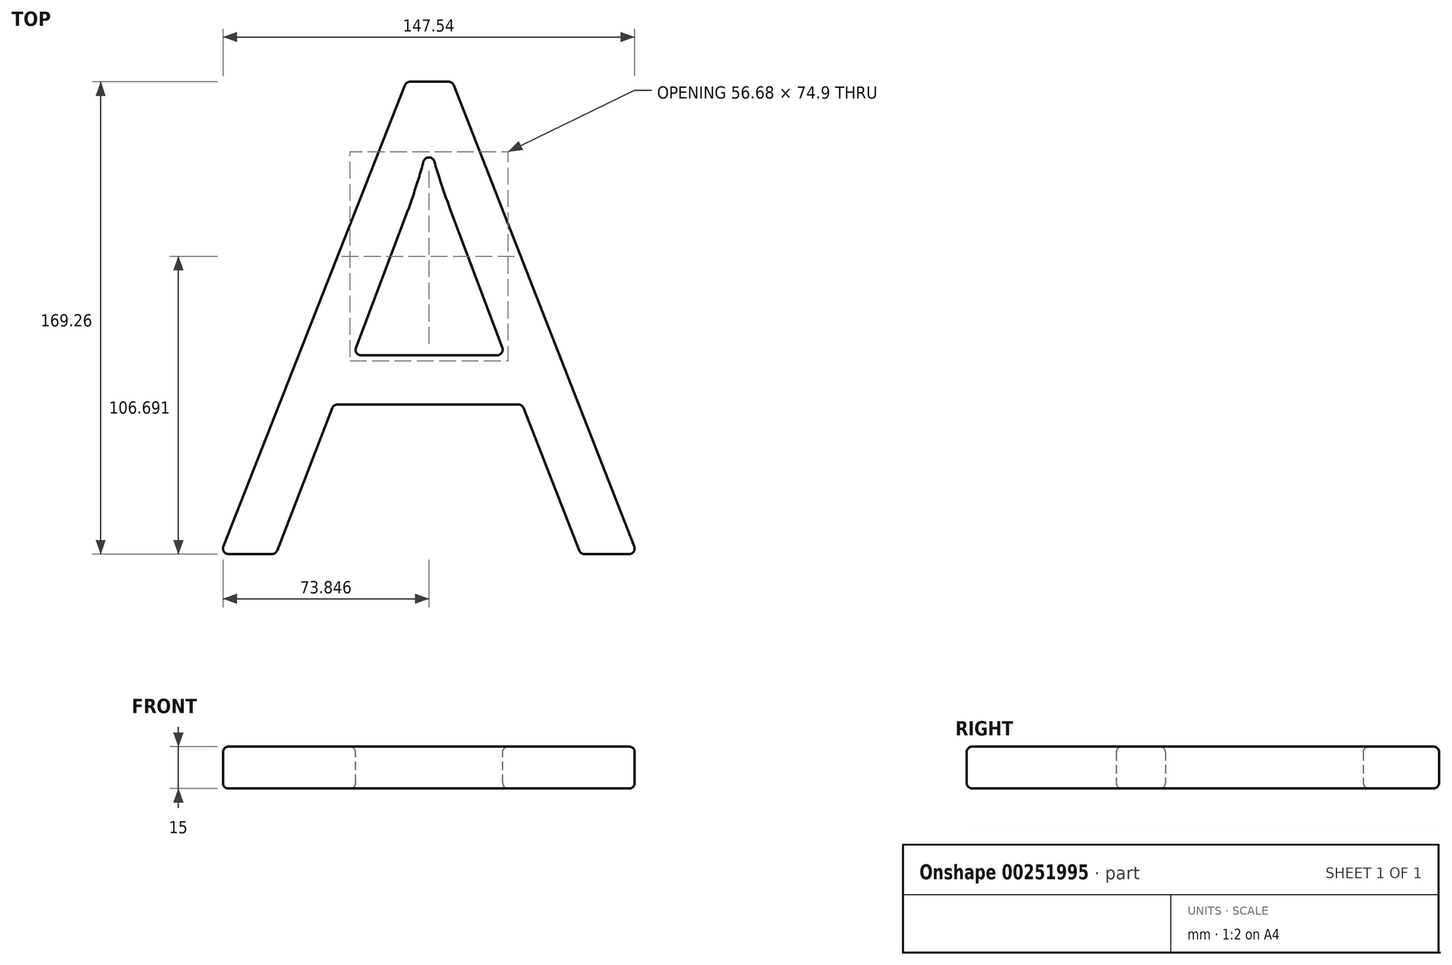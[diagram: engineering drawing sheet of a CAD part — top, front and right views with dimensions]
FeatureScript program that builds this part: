
annotation { "Feature Type Name" : "Feature", "Feature Type Description" : "" }
export const myFeature = defineFeature(function(context is Context, id is Id, definition is map)
    precondition{}
    {
        {
            var Q0;
            Q0=qCreatedBy(makeId("Top.planeOp"),FACE);
            var sketch = newSketch(context, id + "F0", { "sketchPlane" : qUnion([Q0])});
            skLineSegment(sketch, "E0", {"start": v(-70.15, 88.8) * mm, "end": v(95.11, 88.8) * mm, "construction": true});
            skLineSegment(sketch, "E1", {"start": v(-73.3, -81.2) * mm, "end": v(95.11, -81.2) * mm, "construction": true});
            skText(sketch, "E2", { "text": "A", "fontName": "OpenSans-Regular.ttf"});
            const initialGuessF0  = {"E2": [-0.04242, -0.0812, 1, 0, 0.17]};
            skSetInitialGuess(sketch, initialGuessF0);
            skSolve(sketch);
        }
        {
            var Q0;
            Q0 = qSketchRegion(id + "F0", true);
            extrude(context, id + "F1", {"entities" : qUnion([Q0]), "depth" : 15 * mm});
        }
        {
            var Q0;
            Q0=makeQuery(id+"F1.opExtrude","CAP_FACE",FACE,{"disambiguationData":[OSD([sQuery(id+"F0.wireOp",EDGE,"E2.sketch_text.stroke-0"),sQuery(id+"F0.wireOp",EDGE,"E2.sketch_text.stroke-1"),sQuery(id+"F0.wireOp",EDGE,"E2.sketch_text.stroke-2"),sQuery(id+"F0.wireOp",EDGE,"E2.sketch_text.stroke-3"),sQuery(id+"F0.wireOp",EDGE,"E2.sketch_text.stroke-4"),sQuery(id+"F0.wireOp",EDGE,"E2.sketch_text.stroke-5"),sQuery(id+"F0.wireOp",EDGE,"E2.sketch_text.stroke-6"),sQuery(id+"F0.wireOp",EDGE,"E2.sketch_text.stroke-7"),sQuery(id+"F0.wireOp",EDGE,"E2.sketch_text.stroke-8"),sQuery(id+"F0.wireOp",EDGE,"E2.sketch_text.stroke-9"),sQuery(id+"F0.wireOp",EDGE,"E2.sketch_text.stroke-10"),sQuery(id+"F0.wireOp",EDGE,"E2.sketch_text.stroke-11"),sQuery(id+"F0.wireOp",EDGE,"E2.sketch_text.stroke-12")])],"isStart":true});
            var Q1;
            Q1=makeQuery(id+"F1.opExtrude","CAP_FACE",FACE,{"disambiguationData":[OSD([sQuery(id+"F0.wireOp",EDGE,"E2.sketch_text.stroke-0"),sQuery(id+"F0.wireOp",EDGE,"E2.sketch_text.stroke-1"),sQuery(id+"F0.wireOp",EDGE,"E2.sketch_text.stroke-2"),sQuery(id+"F0.wireOp",EDGE,"E2.sketch_text.stroke-3"),sQuery(id+"F0.wireOp",EDGE,"E2.sketch_text.stroke-4"),sQuery(id+"F0.wireOp",EDGE,"E2.sketch_text.stroke-5"),sQuery(id+"F0.wireOp",EDGE,"E2.sketch_text.stroke-6"),sQuery(id+"F0.wireOp",EDGE,"E2.sketch_text.stroke-7"),sQuery(id+"F0.wireOp",EDGE,"E2.sketch_text.stroke-8"),sQuery(id+"F0.wireOp",EDGE,"E2.sketch_text.stroke-9"),sQuery(id+"F0.wireOp",EDGE,"E2.sketch_text.stroke-10"),sQuery(id+"F0.wireOp",EDGE,"E2.sketch_text.stroke-11"),sQuery(id+"F0.wireOp",EDGE,"E2.sketch_text.stroke-12")])],"isStart":false});
            var Q2;
            Q2=makeQuery(id+"F1.opExtrude","SWEPT_FACE",FACE,{"disambiguationData":[OSD([sQuery(id+"F0.wireOp",EDGE,"E2.sketch_text.stroke-1")])]});
            var Q3;
            Q3=makeQuery(id+"F1.opExtrude","SWEPT_EDGE",EDGE,{"disambiguationData":[OSD([sQuery(id+"F0.wireOp",EDGE,"E2.sketch_text.stroke-4"),sQuery(id+"F0.wireOp",EDGE,"E2.sketch_text.stroke-5")])]});
            var Q4;
            Q4=makeQuery(id+"F1.opExtrude","SWEPT_FACE",FACE,{"disambiguationData":[OSD([sQuery(id+"F0.wireOp",EDGE,"E2.sketch_text.stroke-5")])]});
            var Q5;
            Q5=makeQuery(id+"F1.opExtrude","SWEPT_FACE",FACE,{"disambiguationData":[OSD([sQuery(id+"F0.wireOp",EDGE,"E2.sketch_text.stroke-6")])]});
            var Q6;
            Q6=makeQuery(id+"F1.opExtrude","SWEPT_EDGE",EDGE,{"disambiguationData":[OSD([sQuery(id+"F0.wireOp",EDGE,"E2.sketch_text.stroke-5"),sQuery(id+"F0.wireOp",EDGE,"E2.sketch_text.stroke-6")])]});
            var Q7;
            Q7=makeQuery(id+"F1.opExtrude","SWEPT_FACE",FACE,{"disambiguationData":[OSD([sQuery(id+"F0.wireOp",EDGE,"E2.sketch_text.stroke-4")])]});
            var Q8;
            Q8=makeQuery(id+"F1.opExtrude","SWEPT_FACE",FACE,{"disambiguationData":[OSD([sQuery(id+"F0.wireOp",EDGE,"E2.sketch_text.stroke-8")])]});
            var Q9;
            Q9=makeQuery(id+"F1.opExtrude","SWEPT_FACE",FACE,{"disambiguationData":[OSD([sQuery(id+"F0.wireOp",EDGE,"E2.sketch_text.stroke-0")])]});
            var Q10;
            Q10=makeQuery(id+"F1.opExtrude","SWEPT_FACE",FACE,{"disambiguationData":[OSD([sQuery(id+"F0.wireOp",EDGE,"E2.sketch_text.stroke-12")])]});
            var Q11;
            Q11=makeQuery(id+"F1.opExtrude","SWEPT_FACE",FACE,{"disambiguationData":[OSD([sQuery(id+"F0.wireOp",EDGE,"E2.sketch_text.stroke-11")])]});
            var Q12;
            Q12=makeQuery(id+"F1.opExtrude","SWEPT_EDGE",EDGE,{"disambiguationData":[OSD([sQuery(id+"F0.wireOp",EDGE,"E2.sketch_text.stroke-6"),sQuery(id+"F0.wireOp",EDGE,"E2.sketch_text.stroke-7")])]});
            var Q13;
            Q13=makeQuery(id+"F1.opExtrude","SWEPT_EDGE",EDGE,{"disambiguationData":[OSD([sQuery(id+"F0.wireOp",EDGE,"E2.sketch_text.stroke-11"),sQuery(id+"F0.wireOp",EDGE,"E2.sketch_text.stroke-12")])]});
            var Q14;
            Q14=makeQuery(id+"F1.opExtrude","SWEPT_FACE",FACE,{"disambiguationData":[OSD([sQuery(id+"F0.wireOp",EDGE,"E2.sketch_text.stroke-10")])]});
            var Q15;
            Q15=makeQuery(id+"F1.opExtrude","CAP_EDGE",EDGE,{"disambiguationData":[OSD([sQuery(id+"F0.wireOp",EDGE,"E2.sketch_text.stroke-1")])],"isStart":false});
            var Q16;
            Q16=makeQuery(id+"F1.opExtrude","CAP_EDGE",EDGE,{"disambiguationData":[OSD([sQuery(id+"F0.wireOp",EDGE,"E2.sketch_text.stroke-9")])],"isStart":false});
            var Q17;
            Q17=makeQuery(id+"F1.opExtrude","CAP_EDGE",EDGE,{"disambiguationData":[OSD([sQuery(id+"F0.wireOp",EDGE,"E2.sketch_text.stroke-10")])],"isStart":false});
            var Q18;
            Q18=makeQuery(id+"F1.opExtrude","CAP_EDGE",EDGE,{"disambiguationData":[OSD([sQuery(id+"F0.wireOp",EDGE,"E2.sketch_text.stroke-11")])],"isStart":true});
            var Q19;
            Q19=makeQuery(id+"F1.opExtrude","CAP_EDGE",EDGE,{"disambiguationData":[OSD([sQuery(id+"F0.wireOp",EDGE,"E2.sketch_text.stroke-12")])],"isStart":true});
            var Q20;
            Q20=makeQuery(id+"F1.opExtrude","CAP_EDGE",EDGE,{"disambiguationData":[OSD([sQuery(id+"F0.wireOp",EDGE,"E2.sketch_text.stroke-4")])],"isStart":false});
            var Q21;
            Q21=makeQuery(id+"F1.opExtrude","CAP_EDGE",EDGE,{"disambiguationData":[OSD([sQuery(id+"F0.wireOp",EDGE,"E2.sketch_text.stroke-12")])],"isStart":false});
            var Q22;
            Q22=makeQuery(id+"F1.opExtrude","CAP_EDGE",EDGE,{"disambiguationData":[OSD([sQuery(id+"F0.wireOp",EDGE,"E2.sketch_text.stroke-5")])],"isStart":true});
            var Q23;
            Q23=makeQuery(id+"F1.opExtrude","CAP_EDGE",EDGE,{"disambiguationData":[OSD([sQuery(id+"F0.wireOp",EDGE,"E2.sketch_text.stroke-5")])],"isStart":false});
            var Q24;
            Q24=makeQuery(id+"F1.opExtrude","CAP_EDGE",EDGE,{"disambiguationData":[OSD([sQuery(id+"F0.wireOp",EDGE,"E2.sketch_text.stroke-7")])],"isStart":false});
            var Q25;
            Q25=makeQuery(id+"F1.opExtrude","SWEPT_EDGE",EDGE,{"disambiguationData":[OSD([sQuery(id+"F0.wireOp",EDGE,"E2.sketch_text.stroke-0"),sQuery(id+"F0.wireOp",EDGE,"E2.sketch_text.stroke-1")])]});
            var Q26;
            Q26=makeQuery(id+"F1.opExtrude","SWEPT_EDGE",EDGE,{"disambiguationData":[OSD([sQuery(id+"F0.wireOp",EDGE,"E2.sketch_text.stroke-1"),sQuery(id+"F0.wireOp",EDGE,"E2.sketch_text.stroke-2")])]});
            var Q27;
            Q27=makeQuery(id+"F1.opExtrude","SWEPT_EDGE",EDGE,{"disambiguationData":[OSD([sQuery(id+"F0.wireOp",EDGE,"E2.sketch_text.stroke-2"),sQuery(id+"F0.wireOp",EDGE,"E2.sketch_text.stroke-3")])]});
            var Q28;
            Q28=makeQuery(id+"F1.opExtrude","SWEPT_EDGE",EDGE,{"disambiguationData":[OSD([sQuery(id+"F0.wireOp",EDGE,"E2.sketch_text.stroke-3"),sQuery(id+"F0.wireOp",EDGE,"E2.sketch_text.stroke-4")])]});
            var Q29;
            Q29=makeQuery(id+"F1.opExtrude","SWEPT_FACE",FACE,{"disambiguationData":[OSD([sQuery(id+"F0.wireOp",EDGE,"E2.sketch_text.stroke-2")])]});
            var Q30;
            Q30=makeQuery(id+"F1.opExtrude","SWEPT_FACE",FACE,{"disambiguationData":[OSD([sQuery(id+"F0.wireOp",EDGE,"E2.sketch_text.stroke-3")])]});
            var Q31;
            Q31=makeQuery(id+"F1.opExtrude","SWEPT_EDGE",EDGE,{"disambiguationData":[OSD([sQuery(id+"F0.wireOp",EDGE,"E2.sketch_text.stroke-8"),sQuery(id+"F0.wireOp",EDGE,"E2.sketch_text.stroke-12")])]});
            var Q32;
            Q32=makeQuery(id+"F1.opExtrude","SWEPT_EDGE",EDGE,{"disambiguationData":[OSD([sQuery(id+"F0.wireOp",EDGE,"E2.sketch_text.stroke-0"),sQuery(id+"F0.wireOp",EDGE,"E2.sketch_text.stroke-7")])]});
            var Q33;
            Q33=makeQuery(id+"F1.opExtrude","CAP_EDGE",EDGE,{"disambiguationData":[OSD([sQuery(id+"F0.wireOp",EDGE,"E2.sketch_text.stroke-1")])],"isStart":true});
            var Q34;
            Q34=makeQuery(id+"F1.opExtrude","CAP_EDGE",EDGE,{"disambiguationData":[OSD([sQuery(id+"F0.wireOp",EDGE,"E2.sketch_text.stroke-0")])],"isStart":false});
            var Q35;
            Q35=makeQuery(id+"F1.opExtrude","CAP_EDGE",EDGE,{"disambiguationData":[OSD([sQuery(id+"F0.wireOp",EDGE,"E2.sketch_text.stroke-0")])],"isStart":true});
            var Q36;
            Q36=makeQuery(id+"F1.opExtrude","SWEPT_FACE",FACE,{"disambiguationData":[OSD([sQuery(id+"F0.wireOp",EDGE,"E2.sketch_text.stroke-7")])]});
            var Q37;
            Q37=makeQuery(id+"F1.opExtrude","SWEPT_EDGE",EDGE,{"disambiguationData":[OSD([sQuery(id+"F0.wireOp",EDGE,"E2.sketch_text.stroke-10"),sQuery(id+"F0.wireOp",EDGE,"E2.sketch_text.stroke-11")])]});
            var Q38;
            Q38=makeQuery(id+"F1.opExtrude","SWEPT_FACE",FACE,{"disambiguationData":[OSD([sQuery(id+"F0.wireOp",EDGE,"E2.sketch_text.stroke-9")])]});
            var Q39;
            Q39=makeQuery(id+"F1.opExtrude","CAP_EDGE",EDGE,{"disambiguationData":[OSD([sQuery(id+"F0.wireOp",EDGE,"E2.sketch_text.stroke-8")])],"isStart":true});
            var Q40;
            Q40=makeQuery(id+"F1.opExtrude","CAP_EDGE",EDGE,{"disambiguationData":[OSD([sQuery(id+"F0.wireOp",EDGE,"E2.sketch_text.stroke-8")])],"isStart":false});
            var Q41;
            Q41=makeQuery(id+"F1.opExtrude","CAP_EDGE",EDGE,{"disambiguationData":[OSD([sQuery(id+"F0.wireOp",EDGE,"E2.sketch_text.stroke-9")])],"isStart":true});
            var Q42;
            Q42=makeQuery(id+"F1.opExtrude","CAP_EDGE",EDGE,{"disambiguationData":[OSD([sQuery(id+"F0.wireOp",EDGE,"E2.sketch_text.stroke-2")])],"isStart":true});
            var Q43;
            Q43=makeQuery(id+"F1.opExtrude","CAP_EDGE",EDGE,{"disambiguationData":[OSD([sQuery(id+"F0.wireOp",EDGE,"E2.sketch_text.stroke-2")])],"isStart":false});
            var Q44;
            Q44=makeQuery(id+"F1.opExtrude","CAP_EDGE",EDGE,{"disambiguationData":[OSD([sQuery(id+"F0.wireOp",EDGE,"E2.sketch_text.stroke-3")])],"isStart":false});
            var Q45;
            Q45=makeQuery(id+"F1.opExtrude","CAP_EDGE",EDGE,{"disambiguationData":[OSD([sQuery(id+"F0.wireOp",EDGE,"E2.sketch_text.stroke-11")])],"isStart":false});
            var Q46;
            Q46=makeQuery(id+"F1.opExtrude","CAP_EDGE",EDGE,{"disambiguationData":[OSD([sQuery(id+"F0.wireOp",EDGE,"E2.sketch_text.stroke-4")])],"isStart":true});
            var Q47;
            Q47=makeQuery(id+"F1.opExtrude","CAP_EDGE",EDGE,{"disambiguationData":[OSD([sQuery(id+"F0.wireOp",EDGE,"E2.sketch_text.stroke-6")])],"isStart":true});
            var Q48;
            Q48=makeQuery(id+"F1.opExtrude","CAP_EDGE",EDGE,{"disambiguationData":[OSD([sQuery(id+"F0.wireOp",EDGE,"E2.sketch_text.stroke-6")])],"isStart":false});
            var Q49;
            Q49=makeQuery(id+"F1.opExtrude","CAP_EDGE",EDGE,{"disambiguationData":[OSD([sQuery(id+"F0.wireOp",EDGE,"E2.sketch_text.stroke-7")])],"isStart":true});
            var Q50;
            Q50=makeQuery(id+"F1.opExtrude","SWEPT_EDGE",EDGE,{"disambiguationData":[OSD([sQuery(id+"F0.wireOp",EDGE,"E2.sketch_text.stroke-8"),sQuery(id+"F0.wireOp",EDGE,"E2.sketch_text.stroke-9")])]});
            var Q51;
            Q51=makeQuery(id+"F1.opExtrude","SWEPT_EDGE",EDGE,{"disambiguationData":[OSD([sQuery(id+"F0.wireOp",EDGE,"E2.sketch_text.stroke-9"),sQuery(id+"F0.wireOp",EDGE,"E2.sketch_text.stroke-10")])]});
            var Q52;
            Q52=makeQuery(id+"F1.opExtrude","CAP_EDGE",EDGE,{"disambiguationData":[OSD([sQuery(id+"F0.wireOp",EDGE,"E2.sketch_text.stroke-10")])],"isStart":true});
            var Q53;
            Q53=makeQuery(id+"F1.opExtrude","CAP_EDGE",EDGE,{"disambiguationData":[OSD([sQuery(id+"F0.wireOp",EDGE,"E2.sketch_text.stroke-3")])],"isStart":true});
            fillet(context, id + "F2", {"entities" : qUnion([Q0, Q1, Q2, Q3, Q4, Q5, Q6, Q7, Q8, Q9, Q10, Q11, Q12, Q13, Q14, Q15, Q16, Q17, Q18, Q19, Q20, Q21, Q22, Q23, Q24, Q25, Q26, Q27, Q28, Q29, Q30, Q31, Q32, Q33, Q34, Q35, Q36, Q37, Q38, Q39, Q40, Q41, Q42, Q43, Q44, Q45, Q46, Q47, Q48, Q49, Q50, Q51, Q52, Q53]), "radius" : 2 * mm, "tangentPropagation" : true, "allowEdgeOverflow" : false});
        }
    });
